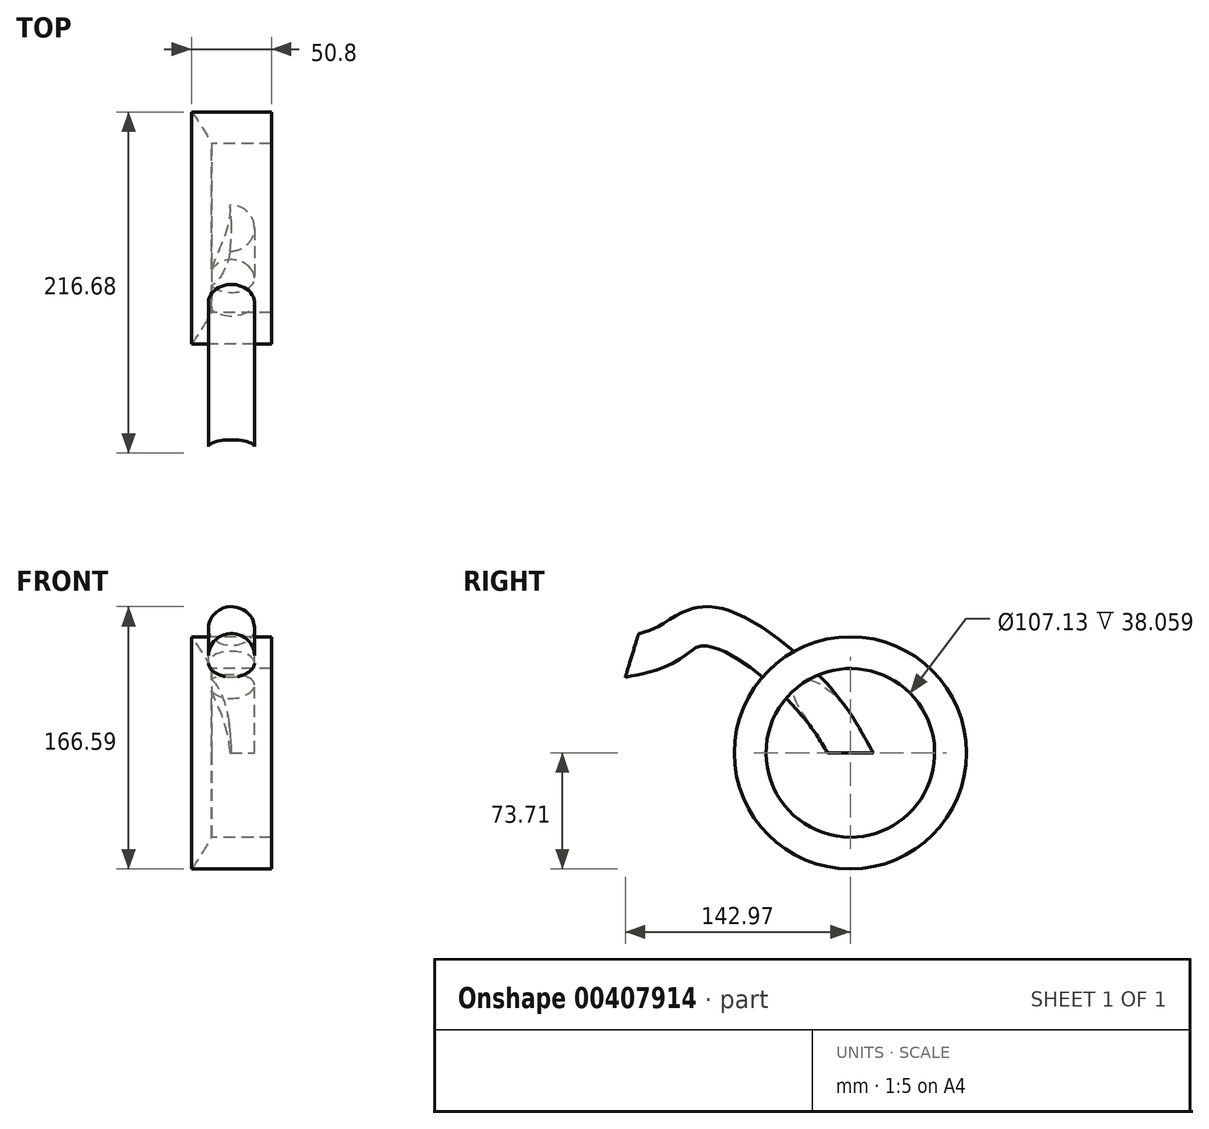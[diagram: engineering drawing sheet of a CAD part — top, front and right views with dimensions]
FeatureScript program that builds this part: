
annotation { "Feature Type Name" : "Feature", "Feature Type Description" : "" }
export const myFeature = defineFeature(function(context is Context, id is Id, definition is map)
    precondition{}
    {
        {
            var Q0;
            Q0=qCreatedBy(makeId("Top.planeOp"),FACE);
            var sketch = newSketch(context, id + "F0", { "sketchPlane" : qUnion([Q0])});
            skCircle(sketch, "E0", {"center": v(0, 0) * mm, "radius": 14.56 * mm});
            skSolve(sketch);
        }
        {
            var Q0;
            Q0=qCreatedBy(makeId("Right.planeOp"),FACE);
            var sketch = newSketch(context, id + "F1", { "sketchPlane" : qUnion([Q0])});
            skFitSpline(sketch, "E1", {"points": [v(0, 0) * mm, v(-26.4, 37.66) * mm, v(-88.48, 79.46) * mm, v(-119.42, 68) * mm, v(-138.05, 62.08) * mm, v(-138.73, 61.93) * mm], "startDerivative": vector(-78.13, 137.3) * mm, "endDerivative": vector(-13.87, -3.12) * mm});
            skSolve(sketch);
        }
        {
            var Q0;
            Q0=makeQuery(id+"F0.imprint","IMPRINT",FACE,{"disambiguationData":[TD([[makeQuery(id+"F0.imprint","IMPRINT",EDGE,{"derivedFrom":sQuery(id+"F0.wireOp",EDGE,"E0")}),1.0]])]});
            var Q1;
            Q1=sQuery(id+"F1.wireOp",EDGE,"E1");
            sweep(context, id + "F2", {"profiles" : qUnion([Q0]), "path" : qUnion([Q1])});
        }
        {
            var Q0;
            Q0=qCreatedBy(makeId("Right.planeOp"),FACE);
            var sketch = newSketch(context, id + "F3", { "sketchPlane" : qUnion([Q0])});
            skCircle(sketch, "E2", {"center": v(0, 0) * mm, "radius": 73.7 * mm});
            skCircle(sketch, "E3", {"center": v(0, 0) * mm, "radius": 53.56 * mm});
            skSolve(sketch);
        }
        {
            var Q0;
            Q0 = qSketchRegion(id + "F3", true);
            extrude(context, id + "F4", {"entities" : qUnion([Q0]), "operationType" : NewBodyOperationType.ADD, "depth" : 25.4 * mm, "hasSecondDirection" : true, "secondDirectionOppositeDirection" : true, "secondDirectionDepth" : 25.4 * mm});
        }
        {
            var Q0;
            Q0=qCreatedBy(makeId("Top.planeOp"),FACE);
            var sketch = newSketch(context, id + "F5", { "sketchPlane" : qUnion([Q0])});
            skLineSegment(sketch, "E4", {"start": v(-119.65, 0) * mm, "end": v(120.23, 0) * mm, "construction": true});
            skArc(sketch, "E5", {"start": v(-25.4, 73.7) * mm, "mid": v(-6.53, 38.98) * mm, "end": v(0, 0) * mm});
            skLineSegment(sketch, "E6", {"start": v(0, 0) * mm, "end": v(0, -60.02) * mm, "construction": true});
            skLineSegment(sketch, "E7.0", {"start": v(-25.4, 73.7) * mm, "end": v(-25.4, 0) * mm});
            skLineSegment(sketch, "E8", {"start": v(0, 0) * mm, "end": v(-25.4, 0) * mm});
            skPoint(sketch, "E9.orphan", {"position": v(-25.4, -73.7) * mm});
            skSolve(sketch);
        }
        {
            var Q0;
            Q0 = qSketchRegion(id + "F5", true);
            var Q1;
            Q1=sQuery(id+"F5.wireOp",EDGE,"E4");
            revolve(context, id + "F6", {"operationType" : NewBodyOperationType.REMOVE, "entities" : qUnion([Q0]), "axis" : qUnion([Q1]), "revolveType" : RevolveType.FULL, "oppositeDirection" : true});
        }
    });
